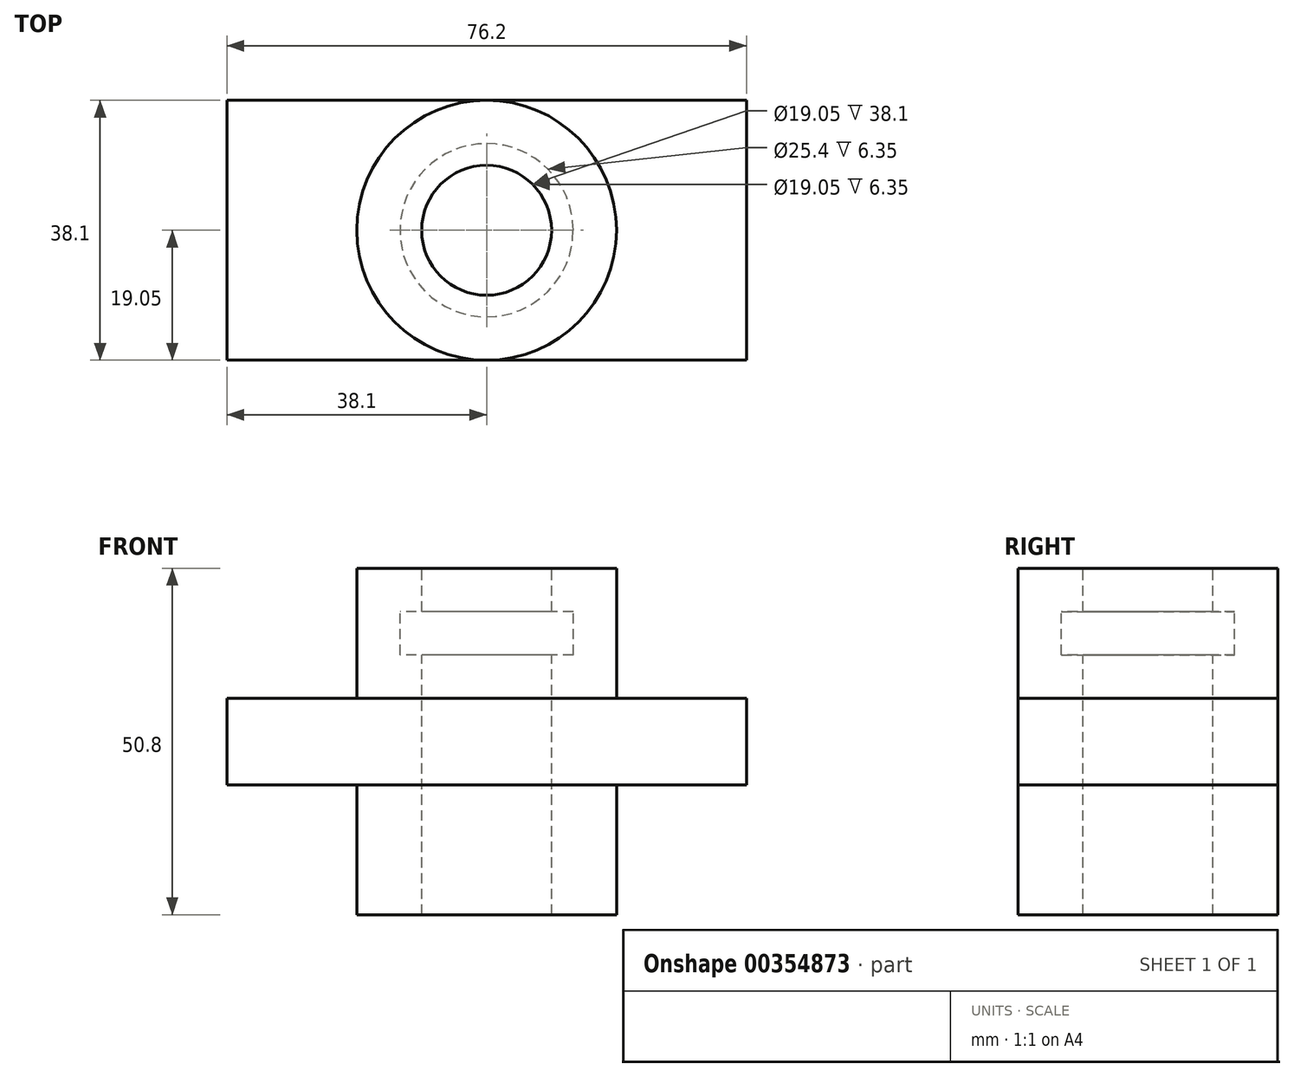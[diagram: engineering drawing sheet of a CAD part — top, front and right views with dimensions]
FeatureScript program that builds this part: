
annotation { "Feature Type Name" : "Feature", "Feature Type Description" : "" }
export const myFeature = defineFeature(function(context is Context, id is Id, definition is map)
    precondition{}
    {
        {
            var Q0;
            Q0=qCreatedBy(makeId("Top.planeOp"),FACE);
            var sketch = newSketch(context, id + "F0", { "sketchPlane" : qUnion([Q0])});
            skCircle(sketch, "E0", {"center": v(0, 0) * mm, "radius": 19.05 * mm});
            skSolve(sketch);
        }
        {
            var Q0;
            Q0 = qSketchRegion(id + "F0", true);
            extrude(context, id + "F1", {"entities" : qUnion([Q0]), "depth" : 19.05 * mm});
        }
        {
            var Q0;
            Q0=makeQuery(id+"F1.opExtrude","CAP_FACE",FACE,{"disambiguationData":[OSD([sQuery(id+"F0.wireOp",EDGE,"E0")])],"isStart":false});
            var sketch = newSketch(context, id + "F2", { "sketchPlane" : qUnion([Q0])});
            skLineSegment(sketch, "E1", {"start": v(0, 19.05) * mm, "end": v(38.1, 19.05) * mm});
            skLineSegment(sketch, "E2", {"start": v(0, 19.05) * mm, "end": v(-38.1, 19.05) * mm});
            skLineSegment(sketch, "E3", {"start": v(0, -19.05) * mm, "end": v(-38.1, -19.05) * mm});
            skLineSegment(sketch, "E4", {"start": v(0, -19.05) * mm, "end": v(38.1, -19.05) * mm});
            skLineSegment(sketch, "E5", {"start": v(-38.1, 19.05) * mm, "end": v(-38.1, -19.05) * mm});
            skLineSegment(sketch, "E6", {"start": v(38.1, 19.05) * mm, "end": v(38.1, -19.05) * mm});
            skSolve(sketch);
        }
        {
            var Q0;
            Q0 = qSketchRegion(id + "F2", true);
            extrude(context, id + "F3", {"entities" : qUnion([Q0]), "operationType" : NewBodyOperationType.ADD, "depth" : 12.7 * mm});
        }
        {
            var Q0;
            Q0=makeQuery(id+"F3.opExtrude","CAP_FACE",FACE,{"disambiguationData":[OSD([sQuery(id+"F2.wireOp",EDGE,"E1"),sQuery(id+"F2.wireOp",EDGE,"E2"),sQuery(id+"F2.wireOp",EDGE,"E3"),sQuery(id+"F2.wireOp",EDGE,"E4"),sQuery(id+"F2.wireOp",EDGE,"E5"),sQuery(id+"F2.wireOp",EDGE,"E6")])],"isStart":false});
            var sketch = newSketch(context, id + "F4", { "sketchPlane" : qUnion([Q0])});
            skCircle(sketch, "E7", {"center": v(0, 0) * mm, "radius": 19.05 * mm});
            skSolve(sketch);
        }
        {
            var Q0;
            Q0 = qSketchRegion(id + "F4", true);
            extrude(context, id + "F5", {"entities" : qUnion([Q0]), "operationType" : NewBodyOperationType.ADD, "depth" : 6.35 * mm});
        }
        {
            var Q0;
            Q0=makeQuery(id+"F5.opExtrude","CAP_FACE",FACE,{"disambiguationData":[OSD([sQuery(id+"F4.wireOp",EDGE,"E7")])],"isStart":false});
            var sketch = newSketch(context, id + "F6", { "sketchPlane" : qUnion([Q0])});
            skCircle(sketch, "E8", {"center": v(0, 0) * mm, "radius": 9.53 * mm});
            skSolve(sketch);
        }
        {
            var Q0;
            Q0 = qSketchRegion(id + "F6", true);
            extrude(context, id + "F7", {"entities" : qUnion([Q0]), "operationType" : NewBodyOperationType.REMOVE, "oppositeDirection" : true, "depth" : 57.15 * mm});
        }
        {
            var Q0;
            Q0=makeQuery(id+"F5.opExtrude","CAP_FACE",FACE,{"disambiguationData":[OSD([sQuery(id+"F4.wireOp",EDGE,"E7")])],"isStart":false});
            var sketch = newSketch(context, id + "F8", { "sketchPlane" : qUnion([Q0])});
            skCircle(sketch, "E9", {"center": v(0, 0) * mm, "radius": 19.05 * mm});
            skSolve(sketch);
        }
        {
            var Q0;
            Q0 = qSketchRegion(id + "F8", true);
            extrude(context, id + "F9", {"entities" : qUnion([Q0]), "operationType" : NewBodyOperationType.ADD, "depth" : 6.35 * mm});
        }
        {
            var Q0;
            Q0=makeQuery(id+"F9.opExtrude","CAP_FACE",FACE,{"disambiguationData":[OSD([sQuery(id+"F8.wireOp",EDGE,"E9")])],"isStart":false});
            var sketch = newSketch(context, id + "F10", { "sketchPlane" : qUnion([Q0])});
            skCircle(sketch, "E10", {"center": v(0, 0) * mm, "radius": 12.7 * mm});
            skSolve(sketch);
        }
        {
            var Q0;
            Q0 = qSketchRegion(id + "F10", true);
            extrude(context, id + "F11", {"entities" : qUnion([Q0]), "operationType" : NewBodyOperationType.REMOVE, "oppositeDirection" : true, "depth" : 6.35 * mm});
        }
        {
            var Q0;
            Q0=makeQuery(id+"F9.opExtrude","CAP_FACE",FACE,{"disambiguationData":[OSD([sQuery(id+"F8.wireOp",EDGE,"E9")])],"isStart":false});
            var sketch = newSketch(context, id + "F12", { "sketchPlane" : qUnion([Q0])});
            skCircle(sketch, "E11", {"center": v(0, 0) * mm, "radius": 19.05 * mm});
            skSolve(sketch);
        }
        {
            var Q0;
            Q0 = qSketchRegion(id + "F12", true);
            extrude(context, id + "F13", {"entities" : qUnion([Q0]), "operationType" : NewBodyOperationType.ADD, "depth" : 6.35 * mm});
        }
        {
            var Q0;
            Q0=makeQuery(id+"F13.opExtrude","CAP_FACE",FACE,{"disambiguationData":[OSD([sQuery(id+"F12.wireOp",EDGE,"E11")])],"isStart":false});
            var sketch = newSketch(context, id + "F14", { "sketchPlane" : qUnion([Q0])});
            skCircle(sketch, "E12", {"center": v(0, 0) * mm, "radius": 9.53 * mm});
            skSolve(sketch);
        }
        {
            var Q0;
            Q0 = qSketchRegion(id + "F14", true);
            extrude(context, id + "F15", {"entities" : qUnion([Q0]), "operationType" : NewBodyOperationType.REMOVE, "oppositeDirection" : true, "depth" : 6.35 * mm});
        }
    });
